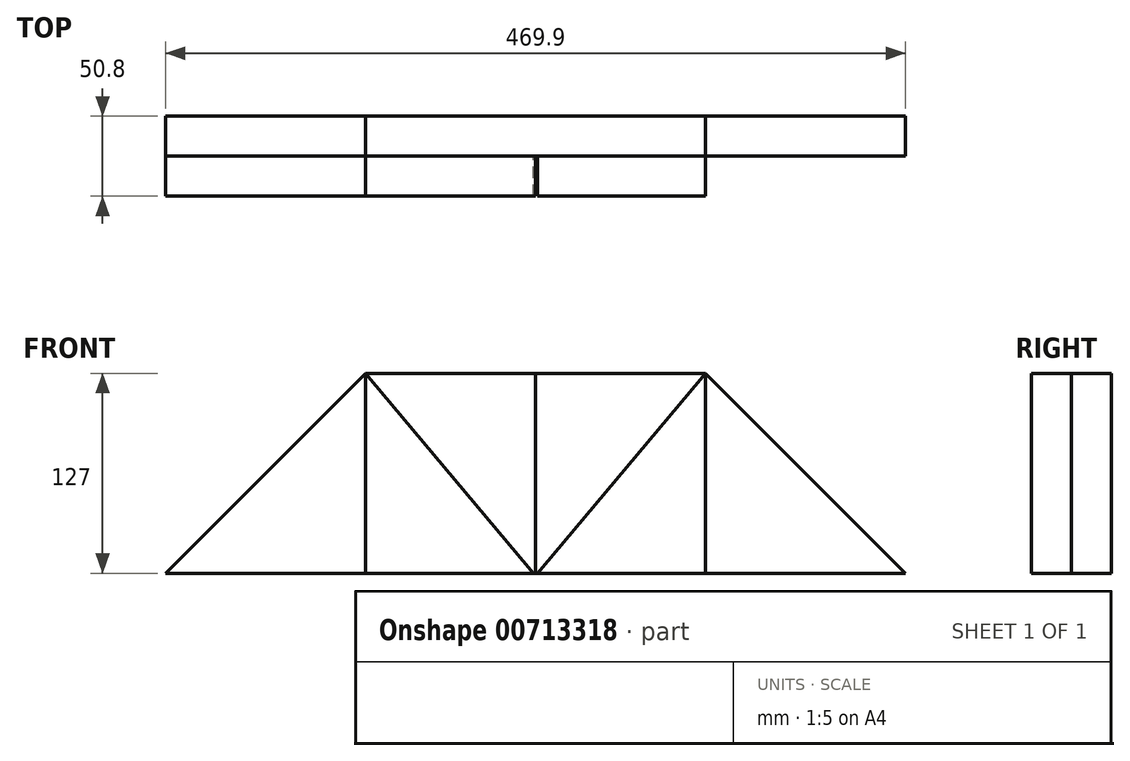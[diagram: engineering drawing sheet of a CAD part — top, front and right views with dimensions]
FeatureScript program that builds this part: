
annotation { "Feature Type Name" : "Feature", "Feature Type Description" : "" }
export const myFeature = defineFeature(function(context is Context, id is Id, definition is map)
    precondition{}
    {
        {
            var Q0;
            Q0=qCreatedBy(makeId("Front.planeOp"),FACE);
            var sketch = newSketch(context, id + "F0", { "sketchPlane" : qUnion([Q0])});
            skLineSegment(sketch, "E0", {"start": v(-203.2, 0) * mm, "end": v(266.7, 0) * mm});
            skLineSegment(sketch, "E1", {"start": v(-203.2, 0) * mm, "end": v(-76.2, 127) * mm});
            skLineSegment(sketch, "E2", {"start": v(-76.2, 127) * mm, "end": v(-76.2, 0) * mm});
            skLineSegment(sketch, "E3", {"start": v(266.7, 0) * mm, "end": v(139.7, 127) * mm});
            skLineSegment(sketch, "E4", {"start": v(139.7, 127) * mm, "end": v(139.7, 0) * mm});
            skLineSegment(sketch, "E5", {"start": v(-76.2, 127) * mm, "end": v(139.7, 127) * mm});
            skLineSegment(sketch, "E6", {"start": v(-76.2, 127) * mm, "end": v(30.37, 0) * mm});
            skLineSegment(sketch, "E7", {"start": v(139.7, 127) * mm, "end": v(33.13, 0) * mm});
            skLineSegment(sketch, "E8", {"start": v(31.75, 127) * mm, "end": v(31.75, 0) * mm});
            skSolve(sketch);
        }
        {
            var Q0;
            {var subQ0=sQuery(id+"F0.wireOp",EDGE,"E1");Q0=makeQuery(id+"F0.imprint","IMPRINT",FACE,{"disambiguationData":[TD([[makeQuery(id+"F0.imprint","IMPRINT",EDGE,{"derivedFrom":subQ0}),-1.0]])]});}
            var Q1;
            {var subQ0=sQuery(id+"F0.wireOp",EDGE,"E6");Q1=makeQuery(id+"F0.imprint","IMPRINT",FACE,{"disambiguationData":[TD([[makeQuery(id+"F0.imprint","IMPRINT",EDGE,{"derivedFrom":subQ0}),1.0]])]});}
            var Q2;
            {var subQ0=sQuery(id+"F0.wireOp",EDGE,"E4");Q2=makeQuery(id+"F0.imprint","IMPRINT",FACE,{"disambiguationData":[TD([[makeQuery(id+"F0.imprint","IMPRINT",EDGE,{"derivedFrom":subQ0}),-1.0]])]});}
            extrude(context, id + "F1", {"entities" : qUnion([Q0, Q1, Q2]), "depth" : 25.4 * mm, "offsetDistance" : 25.4 * mm});
        }
        {
            var Q0;
            Q0 = qSketchRegion(id + "F0", true);
            extrude(context, id + "F2", {"entities" : qUnion([Q0]), "oppositeDirection" : true, "depth" : 25.4 * mm, "offsetDistance" : 25.4 * mm});
        }
    });
